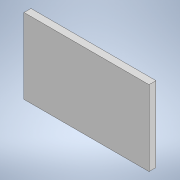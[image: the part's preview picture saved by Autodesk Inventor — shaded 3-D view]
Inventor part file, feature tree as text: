
AUTODESK INVENTOR PART (.ipt)
format: ipt  version: 2020 (Build 240168000, 168)  size: 97,280 bytes
history: native  units: mm
features: extrude x1, sketch x1
ambient origin geometry x8: Origin, YZ Plane, XZ Plane, XY Plane, X Axis, Y Axis, Z Axis, Center Point
bodies: Solid1 (feature_tree)
feature tree (2):
  extrude  "Extrusion1"  Depth=93.0mm
  sketch  "Sketch1"  dims[d0=5.2mm d1=93.0mm d2=56.0mm d3=0.0mm]
